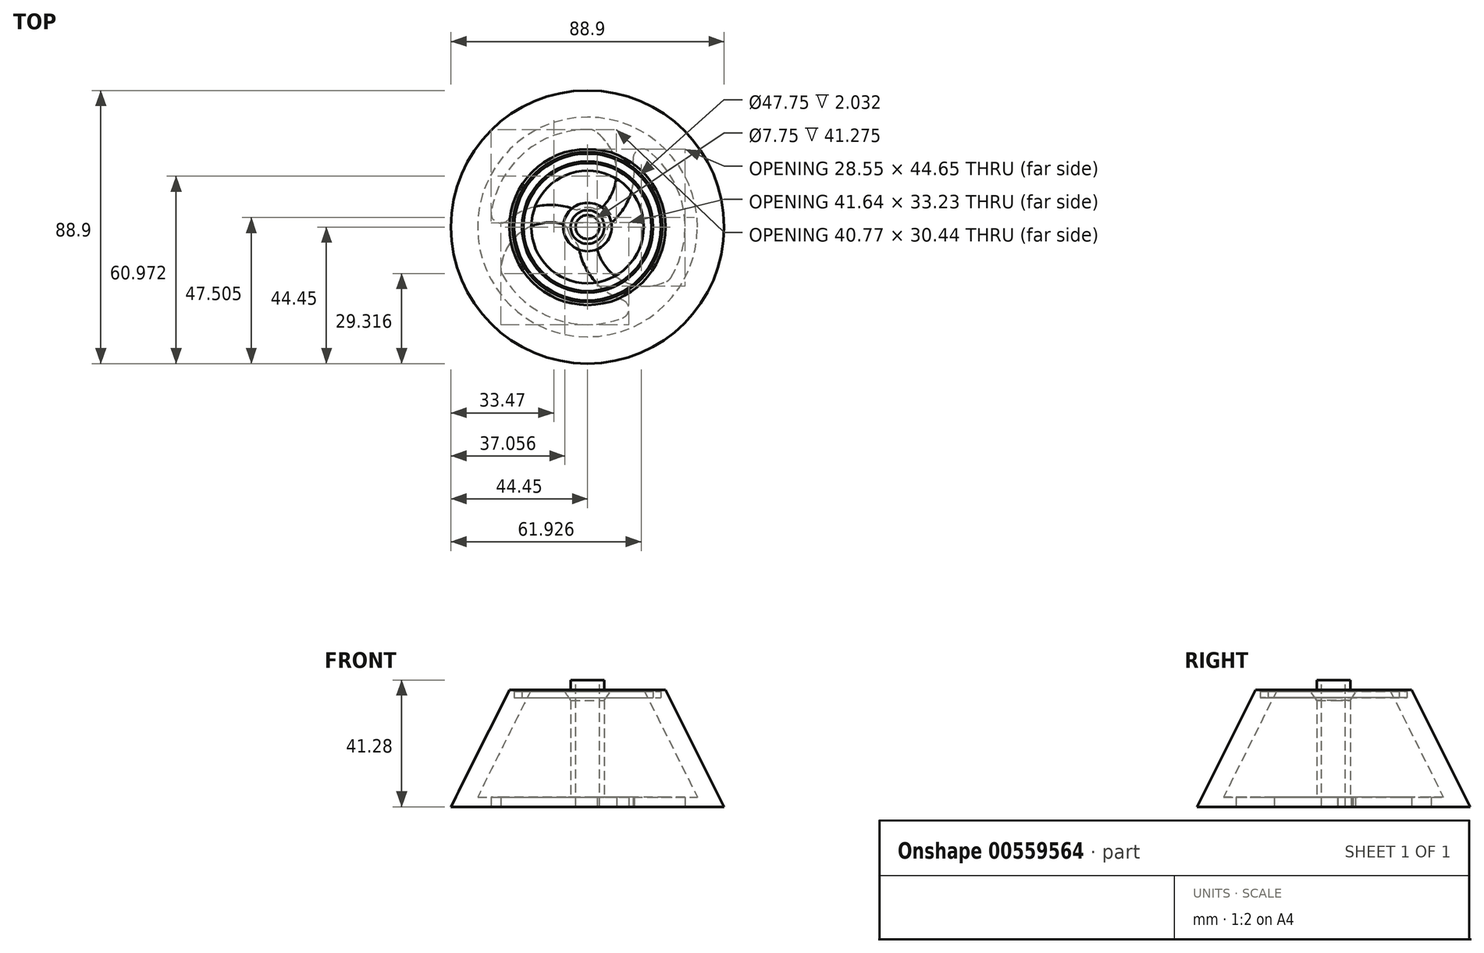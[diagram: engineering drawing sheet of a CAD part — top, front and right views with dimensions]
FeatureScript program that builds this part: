
annotation { "Feature Type Name" : "Feature", "Feature Type Description" : "" }
export const myFeature = defineFeature(function(context is Context, id is Id, definition is map)
    precondition{}
    {
        {
            var Q0;
            Q0=qCreatedBy(makeId("Front.planeOp"),FACE);
            var sketch = newSketch(context, id + "F0", { "sketchPlane" : qUnion([Q0])});
            skLineSegment(sketch, "E0", {"start": v(0, 0) * mm, "end": v(0, 42.5) * mm, "construction": true});
            skLineSegment(sketch, "E1", {"start": v(-25.4, 38.1) * mm, "end": v(-44.45, 0) * mm});
            skLineSegment(sketch, "E2", {"start": v(-44.45, 0) * mm, "end": v(0, 0) * mm});
            skLineSegment(sketch, "E3", {"start": v(-18.3, 38.1) * mm, "end": v(-35.76, 3.18) * mm});
            skLineSegment(sketch, "E4", {"start": v(-35.76, 3.18) * mm, "end": v(-5.46, 3.18) * mm});
            skLineSegment(sketch, "E5", {"start": v(-5.46, 41.28) * mm, "end": v(-5.46, 38.1) * mm});
            skLineSegment(sketch, "E6", {"start": v(-3.87, 42.98) * mm, "end": v(-3.87, -6.9) * mm, "construction": true});
            skLineSegment(sketch, "E7", {"start": v(0, 41.28) * mm, "end": v(0, 0) * mm});
            skLineSegment(sketch, "E8", {"start": v(-5.46, 41.28) * mm, "end": v(0, 41.28) * mm});
            skLineSegment(sketch, "E9", {"start": v(-25.4, 38.1) * mm, "end": v(-24.38, 38.1) * mm});
            skLineSegment(sketch, "E10", {"start": v(-23.88, 37.6) * mm, "end": v(-23.88, 35.56) * mm});
            skLineSegment(sketch, "E11", {"start": v(-23.88, 35.56) * mm, "end": v(-21.34, 35.56) * mm});
            skLineSegment(sketch, "E12", {"start": v(-21.34, 35.56) * mm, "end": v(-21.34, 37.6) * mm});
            skLineSegment(sketch, "E13.trimOffspring", {"start": v(-20.83, 38.1) * mm, "end": v(-18.3, 38.1) * mm});
            skLineSegment(sketch, "E14", {"start": v(-5.46, 38.1) * mm, "end": v(-7.87, 38.1) * mm});
            skLineSegment(sketch, "E15", {"start": v(-7.87, 38.1) * mm, "end": v(-5.46, 34.65) * mm});
            skLineSegment(sketch, "E16.trimOffspring", {"start": v(-5.46, 34.65) * mm, "end": v(-5.46, 3.18) * mm});
            skLineSegment(sketch, "E17", {"start": v(-24.38, 38.1) * mm, "end": v(-23.88, 37.6) * mm});
            skLineSegment(sketch, "E18", {"start": v(-21.34, 37.6) * mm, "end": v(-20.83, 38.1) * mm});
            skPoint(sketch, "E19.orphan", {"position": v(-21.34, 38.1) * mm});
            skSolve(sketch);
        }
        {
            var Q0;
            Q0=makeQuery(id+"F0.imprint","IMPRINT",FACE,{"disambiguationData":[TD([[makeQuery(id+"F0.imprint","IMPRINT",EDGE,{"derivedFrom":sQuery(id+"F0.wireOp",EDGE,"E1")}),1.0]])]});
            var Q1;
            Q1=sQuery(id+"F0.wireOp",EDGE,"E0");
            revolve(context, id + "F1", {"entities" : qUnion([Q0]), "axis" : qUnion([Q1]), "revolveType" : RevolveType.FULL});
        }
        {
            var Q0;
            Q0=makeQuery(id+"F1.opRevolve","SWEPT_FACE",FACE,{"disambiguationData":[OSD([sQuery(id+"F0.wireOp",EDGE,"E8")])]});
            var sketch = newSketch(context, id + "F2", { "sketchPlane" : qUnion([Q0])});
            skCircle(sketch, "E20", {"center": v(0, 0) * mm, "radius": 3.87 * mm});
            skSolve(sketch);
        }
        {
            var Q0;
            Q0=makeQuery(id+"F2.imprint","IMPRINT",FACE,{"disambiguationData":[TD([[makeQuery(id+"F2.imprint","IMPRINT",EDGE,{"derivedFrom":sQuery(id+"F2.wireOp",EDGE,"E20")}),1.0]])]});
            extrude(context, id + "F3", {"entities" : qUnion([Q0]), "operationType" : NewBodyOperationType.REMOVE, "endBound" : BoundingType.THROUGH_ALL, "oppositeDirection" : true, "depth" : 25.4 * mm, "offsetDistance" : 25.4 * mm});
        }
        {
            var Q0;
            Q0=makeQuery(id+"F1.opRevolve","SWEPT_FACE",FACE,{"disambiguationData":[OSD([sQuery(id+"F0.wireOp",EDGE,"E2")])]});
            var sketch = newSketch(context, id + "F4", { "sketchPlane" : qUnion([Q0])});
            skArc(sketch, "E21", {"start": v(-3.95, 4.97) * mm, "mid": v(-0.2, -6.35) * mm, "end": v(4.25, 4.72) * mm});
            skArc(sketch, "E22", {"start": v(11.39, 29.64) * mm, "mid": v(-20.37, -24.35) * mm, "end": v(27.16, 16.44) * mm});
            skArc(sketch, "E23", {"start": v(23.28, 21.59) * mm, "mid": v(8.33, 19.02) * mm, "end": v(0, 6.35) * mm, "construction": true});
            skArc(sketch, "E24.0", {"start": v(11.33, 23.69) * mm, "mid": v(2, 17.2) * mm, "end": v(-2.8, 6.9) * mm});
            skArc(sketch, "E25.0", {"start": v(25.83, 17.65) * mm, "mid": v(12.4, 17.97) * mm, "end": v(3.36, 8.05) * mm});
            skPoint(sketch, "E26.visualSharp", {"position": v(-3, 5.6) * mm});
            skArc(sketch, "E26.filletArc", {"start": v(-3.95, 4.97) * mm, "mid": v(-3.2, 5.83) * mm, "end": v(-2.8, 6.9) * mm});
            skPoint(sketch, "E27.visualSharp", {"position": v(2.79, 5.7) * mm});
            skArc(sketch, "E27.filletArc", {"start": v(3.36, 8.05) * mm, "mid": v(3.31, 6.25) * mm, "end": v(4.25, 4.72) * mm});
            skPoint(sketch, "E28.visualSharp", {"position": v(19.6, 24.97) * mm});
            skArc(sketch, "E28.filletArc", {"start": v(11.33, 23.69) * mm, "mid": v(13.42, 26.64) * mm, "end": v(11.39, 29.64) * mm});
            skPoint(sketch, "E29.visualSharp", {"position": v(26.68, 17.2) * mm});
            skArc(sketch, "E29.filletArc", {"start": v(27.16, 16.44) * mm, "mid": v(26.58, 17.14) * mm, "end": v(25.83, 17.65) * mm});
            skArc(sketch, "E30.1.0", {"start": v(-26.18, -2.03) * mm, "mid": v(-15.9, -6.86) * mm, "end": v(-4.57, -5.88) * mm});
            skArc(sketch, "E30.1.1", {"start": v(-26.18, -2.03) * mm, "mid": v(-29.78, -1.7) * mm, "end": v(-31.36, -4.96) * mm});
            skArc(sketch, "E30.1.2", {"start": v(-28.2, 13.54) * mm, "mid": v(-21.77, 1.76) * mm, "end": v(-8.65, -1.12) * mm});
            skArc(sketch, "E30.1.3", {"start": v(-2.33, -5.9) * mm, "mid": v(-3.45, -5.69) * mm, "end": v(-4.57, -5.88) * mm});
            skArc(sketch, "E30.1.4", {"start": v(-8.65, -1.12) * mm, "mid": v(-7.07, -0.26) * mm, "end": v(-6.21, 1.32) * mm});
            skArc(sketch, "E30.1.5", {"start": v(-27.82, 15.3) * mm, "mid": v(-28.14, 14.45) * mm, "end": v(-28.2, 13.54) * mm});
            skArc(sketch, "E30.2.0", {"start": v(14.85, -21.65) * mm, "mid": v(13.88, -10.33) * mm, "end": v(7.38, -1.02) * mm});
            skArc(sketch, "E30.2.1", {"start": v(14.85, -21.65) * mm, "mid": v(16.36, -24.95) * mm, "end": v(19.97, -24.68) * mm});
            skArc(sketch, "E30.2.2", {"start": v(2.37, -31.2) * mm, "mid": v(9.36, -19.73) * mm, "end": v(5.3, -6.93) * mm});
            skArc(sketch, "E30.2.3", {"start": v(6.28, 0.94) * mm, "mid": v(6.65, -0.14) * mm, "end": v(7.38, -1.02) * mm});
            skArc(sketch, "E30.2.4", {"start": v(5.3, -6.93) * mm, "mid": v(3.76, -6) * mm, "end": v(1.96, -6.04) * mm});
            skArc(sketch, "E30.2.5", {"start": v(0.66, -31.74) * mm, "mid": v(1.55, -31.6) * mm, "end": v(2.37, -31.2) * mm});
            skSolve(sketch);
        }
        {
            var Q0;
            Q0=makeQuery(id+"F4.imprint","IMPRINT",FACE,{"disambiguationData":[TD([[makeQuery(id+"F4.imprint","IMPRINT",EDGE,{"derivedFrom":sQuery(id+"F4.wireOp",EDGE,"E24.0")}),-1.0]])]});
            var Q1;
            Q1=makeQuery(id+"F4.imprint","IMPRINT",FACE,{"disambiguationData":[TD([[makeQuery(id+"F4.imprint","IMPRINT",EDGE,{"derivedFrom":sQuery(id+"F4.wireOp",EDGE,"E30.1.0")}),-1.0]])]});
            var Q2;
            Q2=makeQuery(id+"F4.imprint","IMPRINT",FACE,{"disambiguationData":[TD([[makeQuery(id+"F4.imprint","IMPRINT",EDGE,{"derivedFrom":sQuery(id+"F4.wireOp",EDGE,"E25.0")}),1.0]])]});
            extrude(context, id + "F5", {"entities" : qUnion([Q0, Q1, Q2]), "operationType" : NewBodyOperationType.REMOVE, "oppositeDirection" : true, "depth" : 3.17 * mm, "offsetDistance" : 25.4 * mm});
        }
    });
